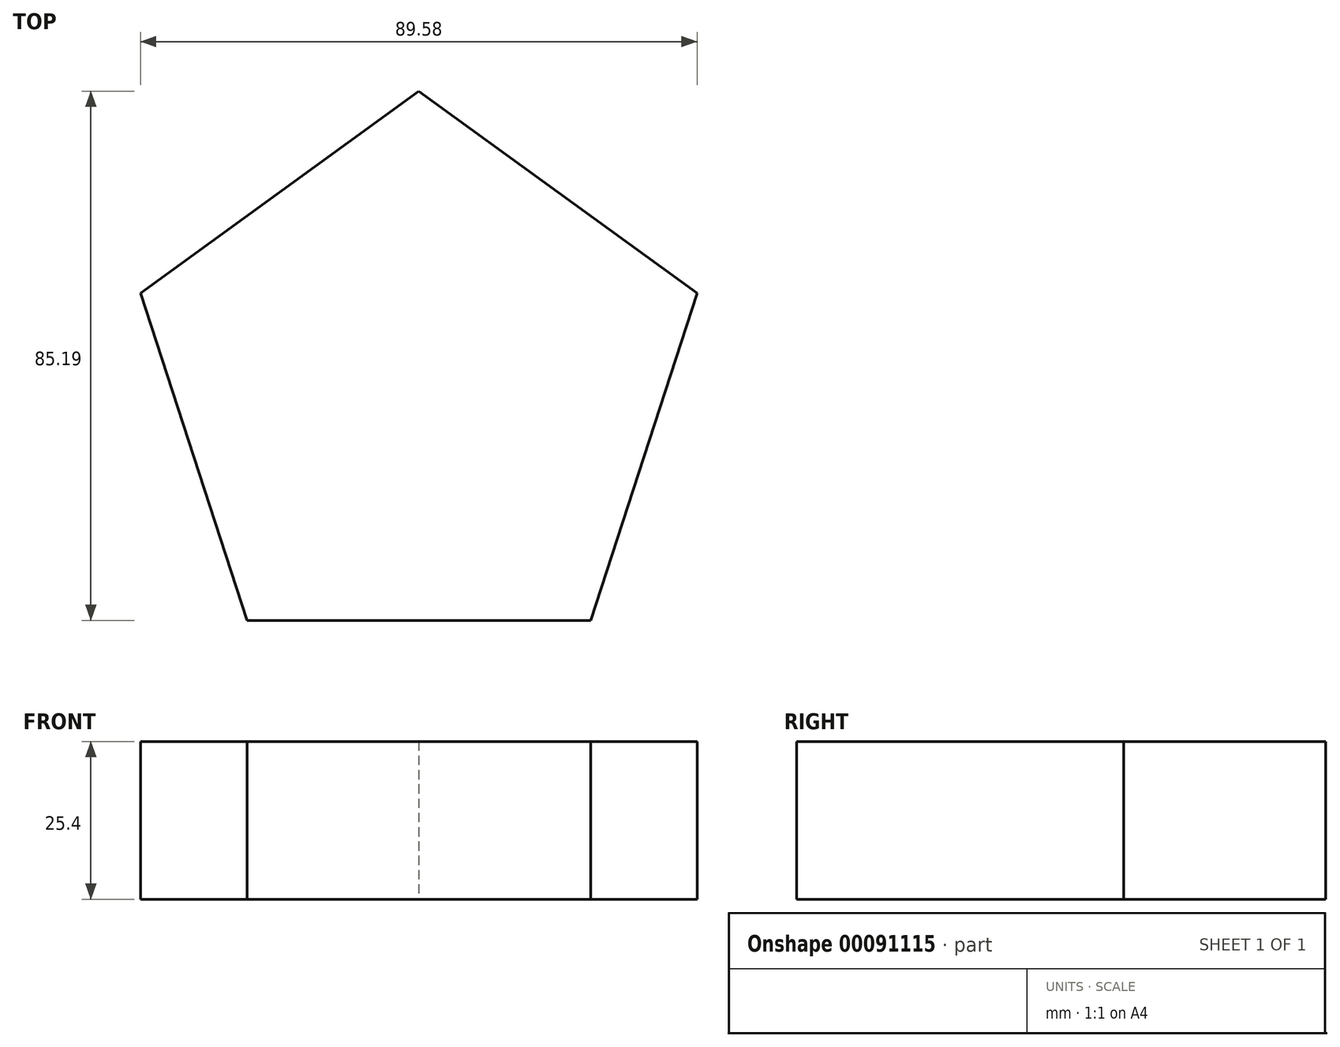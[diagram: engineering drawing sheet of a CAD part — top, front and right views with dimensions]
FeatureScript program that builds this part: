
annotation { "Feature Type Name" : "Feature", "Feature Type Description" : "" }
export const myFeature = defineFeature(function(context is Context, id is Id, definition is map)
    precondition{}
    {
        {
            var Q0;
            Q0=qCreatedBy(makeId("Top.planeOp"),FACE);
            var sketch = newSketch(context, id + "F0", { "sketchPlane" : qUnion([Q0])});
            skCircle(sketch, "E0.cCircle", {"center": v(0, 0) * mm, "radius": 38.1 * mm, "construction": true});
            skLineSegment(sketch, "E0.0", {"start": v(-44.79, 14.55) * mm, "end": v(0, 47.1) * mm});
            skLineSegment(sketch, "E0.1", {"start": v(0, 47.1) * mm, "end": v(44.79, 14.55) * mm});
            skLineSegment(sketch, "E0.2", {"start": v(44.79, 14.55) * mm, "end": v(27.68, -38.1) * mm});
            skLineSegment(sketch, "E0.3", {"start": v(27.68, -38.1) * mm, "end": v(-27.68, -38.1) * mm});
            skLineSegment(sketch, "E0.4", {"start": v(-27.68, -38.1) * mm, "end": v(-44.79, 14.55) * mm});
            skPoint(sketch, "E0.0.midPoint", {"position": v(-22.4, 30.82) * mm});
            skSolve(sketch);
        }
        {
            var Q0;
            Q0=makeQuery(id+"F0.imprint","IMPRINT",FACE,{"disambiguationData":[TD([[makeQuery(id+"F0.imprint","IMPRINT",EDGE,{"derivedFrom":sQuery(id+"F0.wireOp",EDGE,"E0.0")}),-1.0]])]});
            extrude(context, id + "F1", {"entities" : qUnion([Q0]), "depth" : 25.4 * mm});
        }
    });
